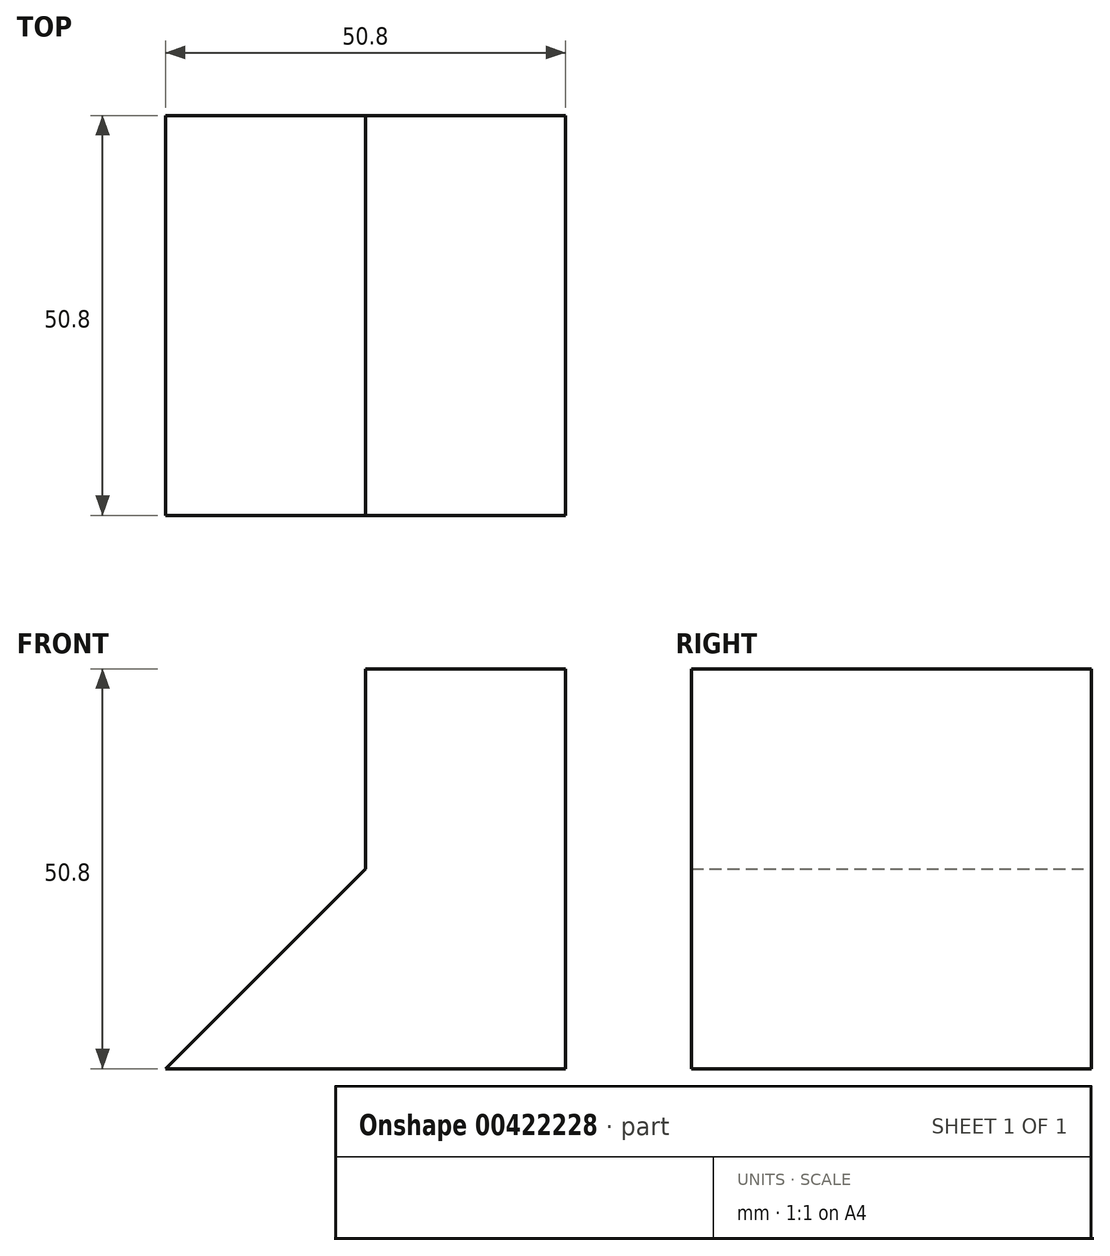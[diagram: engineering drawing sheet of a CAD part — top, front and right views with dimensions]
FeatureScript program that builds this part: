
annotation { "Feature Type Name" : "Feature", "Feature Type Description" : "" }
export const myFeature = defineFeature(function(context is Context, id is Id, definition is map)
    precondition{}
    {
        {
            var Q0;
            Q0=qCreatedBy(makeId("Front.planeOp"),FACE);
            var sketch = newSketch(context, id + "F0", { "sketchPlane" : qUnion([Q0])});
            skLineSegment(sketch, "E0", {"start": v(-5.62, 11.85) * mm, "end": v(-5.62, 37.25) * mm});
            skLineSegment(sketch, "E1", {"start": v(-5.62, 37.25) * mm, "end": v(19.78, 37.25) * mm});
            skLineSegment(sketch, "E2", {"start": v(19.78, 37.25) * mm, "end": v(19.78, -13.55) * mm});
            skLineSegment(sketch, "E3", {"start": v(19.78, -13.55) * mm, "end": v(-31.02, -13.55) * mm});
            skLineSegment(sketch, "E4", {"start": v(-31.02, -13.55) * mm, "end": v(-5.62, 11.85) * mm});
            skSolve(sketch);
        }
        {
            var Q0;
            Q0 = qSketchRegion(id + "F0", true);
            extrude(context, id + "F1", {"entities" : qUnion([Q0]), "depth" : 50.8 * mm});
        }
    });
